# Revit family: Accessory-Tissue_Holder-KOHLER-LOURE-K-11584T_1
name_source: partatom
category: Specialty Equipment
units: mm (PartAtom-declared; Revit-internal decimal feet)

## family parameters
Cut with Voids When Loaded = No
Host = Face
OmniClass Number = 23.31.25.21
OmniClass Title = Toilet Paper Dispensers
Part Type = Normal
Room Calculation Point = No
Round Connector Dimension = Use Diameter
Shared = No

## types (4) — shared parameters
ADA Compliant = No
Assembly Code = C1030200
Date Modified = 11/21/2022
Default Elevation = 42"
Height = 3 1/8"
Length = 4 1/4"
Manufacturer = Kohler Co.
Master Format 2014 = 10 28 00
Master Format 2014 Name = Toilet, Bath, and Laundry Accessories
Material = Premium Metal Construction
Product Name = LOURE
URL = http://www.kohler.com.cn
WaterSense Certified = No
Width = 6 1/8"

## per-type parameters (varying)
| type | Description | Finish | Model | Product Documentation Link | Product Page URL | Type |
| B, 2BL-Black | Covered Tissue Paper Holder | KOHLER-Metal-2BL-Black | K-11584T-B-2BL |  |  | 1 |
| B, BL-Matte Black | Covered Tissue Paper Holder | Kohler-Metal-BL-Matte_Black | K-11584T-B-BL |  |  | 2 |
| B, CP-Polished Chrome | Covered Tissue Paper Holder | Kohler-Metal-CP-Polished_Chrome | K-11584T-B-CP |  |  | 3 |
| CP-Polished Chrome | Toilet paper holder (with cover) | Kohler-Metal-CP-Polished_Chrome | K-11584T-CP | https://files.kohler.com.cn | https://www.kohler.com.cn | 4 |

## geometry (parser evidence)
native form markers: Sweep x5
no freeform markers — native parametric forms only
